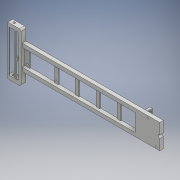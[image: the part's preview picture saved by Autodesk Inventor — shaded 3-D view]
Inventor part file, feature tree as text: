
AUTODESK INVENTOR PART (.ipt)
format: ipt  version: 2018 (Build 220112000, 112)  size: 334,336 bytes
history: native  units: mm
features: sketch x20, extrude x14, fillet x6, hole x4
ambient origin geometry x8: Origin, YZ Plane, XZ Plane, XY Plane, X Axis, Y Axis, Z Axis, Center Point
bodies: Solid1 (feature_tree)
feature tree (44):
  extrude  "Extrusion1"  Depth=50.0mm
  hole  "Hole1"  [1 undecoded]
  hole  "Hole2"  [1 undecoded]
  extrude  "Extrusion2"  Depth=25.0mm
  extrude  "Extrusion3"  Depth=25.0mm
  extrude  "Extrusion4"  Depth=5.0mm
  sketch  "Sketch7"  dims[d25=10.0mm d26=5.0mm]
  extrude  "Extrusion5"  Depth=5.0mm
  extrude  "Extrusion6"  Depth=35.0mm
  extrude  "Extrusion7"  Depth=35.0mm
  extrude  "Extrusion8"  Depth=35.0mm
  extrude  "Extrusion9"  Depth=2.0mm TaperAngle=0.0deg
  extrude  "Extrusion10"  Depth=7.5mm TaperAngle=0.0deg
  extrude  "Extrusion11"  Depth=10.0mm
  extrude  "Extrusion12"  Depth=7.5mm
  fillet  "Fillet1"  Radius=7.5mm
  fillet  "Fillet2"  Radius=25.0mm
  fillet  "Fillet3"  Radius=3.0mm
  fillet  "Fillet4"  Radius=3.2mm
  fillet  "Fillet5"  Radius=2.1mm
  fillet  "Fillet6"  Radius=5.5mm
  extrude  "Extrusion13"  Depth=92.5mm TaperAngle=0.0deg
  sketch  "Sketch17"  dims[d58=4.25mm d59=241.0mm d60=0.0mm]
  hole  "Hole3"  [1 undecoded]
  hole  "Hole4"  [1 undecoded]
  extrude  "Extrusion14"  Depth=5.0mm
  sketch  "Sketch1"  dims[d0=50.0mm d1=50.0mm]
  sketch  "Sketch2"  dims[d2=240.0mm d3=7.5mm]
  sketch  "Sketch3"  dims[d4=7.5mm d5=7.5mm d6=0.0mm]
  sketch  "Sketch4"  dims[d7=6.35mm d8=6.0mm d9=4.0mm d10=2.0mm d11=90.0deg d12=8.0mm d13=20.594885mm d14=25.0mm]
  sketch  "Sketch5"  dims[d15=3.3mm d16=6.0mm d17=4.0mm d18=2.0mm d19=90.0deg d20=8.0mm d21=20.594885mm d22=25.0mm]
  sketch  "Sketch6"  dims[d23=180.0deg d24=5.0mm]
  sketch  "Sketch8"  dims[d27=17.5mm d28=0.0mm d30=35.0mm]
  sketch  "Sketch9"  dims[d31=35.0mm d32=35.0mm]
  sketch  "Sketch10"  dims[d33=35.0mm d34=35.0mm]
  sketch  "Sketch11"  dims[d35=35.0mm d36=2.0mm d37=0.0mm]
  sketch  "Sketch12"  dims[d38=10.0mm d39=7.5mm d40=0.0mm]
  sketch  "Sketch13"  dims[d41=100.0mm d42=10.0mm]
  sketch  "Sketch14"  dims[d43=7.5mm d44=0.0mm d45=7.5mm d46=7.5mm d47=25.0mm d48=0.0mm d49=3.0mm d50=3.2mm d51=2.1mm d52=5.5mm]
  sketch  "Sketch15"  dims[d53=3.3mm d54=92.5mm d55=0.0mm]
  sketch  "Sketch16"  dims[d56=5.5mm d57=3.3mm]
  sketch  "Sketch18"  dims[d61=4.44mm d62=5.0mm]
  sketch  "Sketch19"  dims[d63=2.5mm]
  sketch  "Sketch20"  dims[d64=91.25mm d65=0.0mm d66=30.0mm d67=6.35mm d68=3.8mm d69=0.0mm d70=2.5mm d71=14.55mm d72=0.0mm d73=14.55mm d74=0.0mm d75=1.0mm d76=1.0mm d77=3.25mm d78=3.25mm d79=3.25mm d80=3.25mm d81=35.0mm d82=10.0mm d83=2.0mm d84=0.0mm d85=3.6mm d86=3.6mm d87=3.3mm d88=6.0mm d89=4.0mm d90=2.0mm d91=90.0deg d92=15.0mm d93=20.594885mm d94=3.3mm d95=6.0mm d96=4.0mm d97=2.0mm d98=90.0deg d99=15.0mm d100=20.594885mm d101=6.0mm d102=20.0mm d103=0.0mm]
note: 4 required parameter values undecoded (feature->parameter linkage not recoverable at this tier; creation-order binding heuristic only, values carry confidence <= 0.55)
